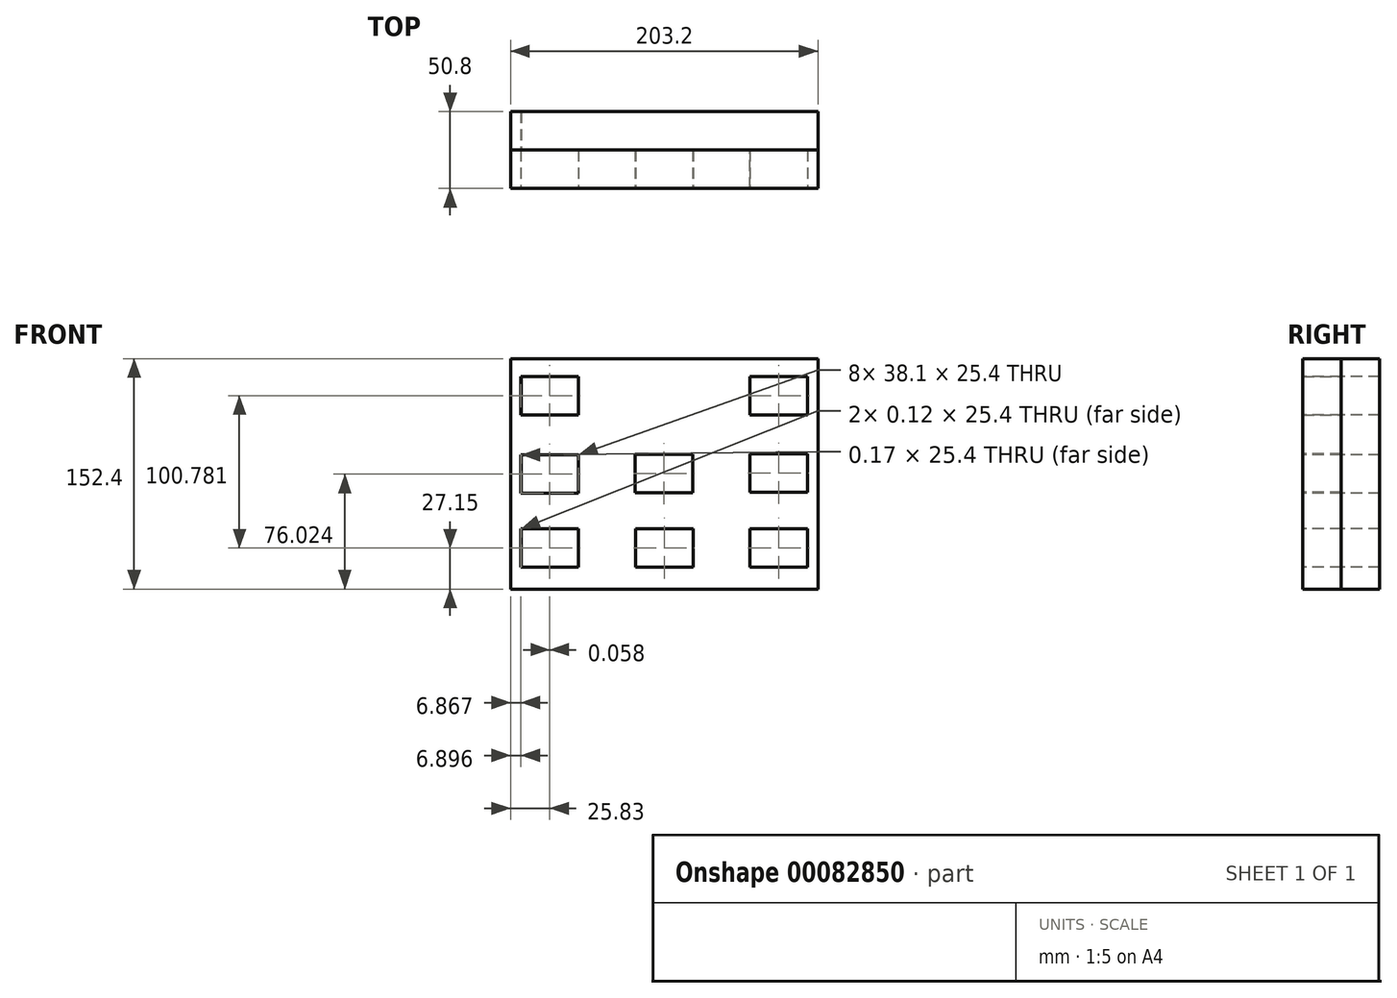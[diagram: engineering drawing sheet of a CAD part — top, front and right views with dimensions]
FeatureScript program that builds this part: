
annotation { "Feature Type Name" : "Feature", "Feature Type Description" : "" }
export const myFeature = defineFeature(function(context is Context, id is Id, definition is map)
    precondition{}
    {
        {
            var Q0;
            Q0=qCreatedBy(makeId("Front.planeOp"),FACE);
            var sketch = newSketch(context, id + "F0", { "sketchPlane" : qUnion([Q0])});
            skLineSegment(sketch, "E0.bottom", {"start": v(-101.6, 76.2) * mm, "end": v(101.6, 76.2) * mm});
            skLineSegment(sketch, "E0.top", {"start": v(-101.6, -76.2) * mm, "end": v(101.6, -76.2) * mm});
            skLineSegment(sketch, "E0.left", {"start": v(-101.6, 76.2) * mm, "end": v(-101.6, -76.2) * mm});
            skLineSegment(sketch, "E0.right", {"start": v(101.6, 76.2) * mm, "end": v(101.6, -76.2) * mm});
            skPoint(sketch, "E0.middle", {"position": v(0, 0) * mm});
            skSolve(sketch);
        }
        {
            var Q0;
            Q0 = qSketchRegion(id + "F0", true);
            extrude(context, id + "F1", {"entities" : qUnion([Q0]), "depth" : 25.4 * mm});
        }
        {
            var Q0;
            Q0=makeQuery(id+"F1.opExtrude","CAP_FACE",FACE,{"disambiguationData":[OSD([sQuery(id+"F0.wireOp",EDGE,"E0.bottom"),sQuery(id+"F0.wireOp",EDGE,"E0.top"),sQuery(id+"F0.wireOp",EDGE,"E0.left"),sQuery(id+"F0.wireOp",EDGE,"E0.right")])],"isStart":false});
            var sketch = newSketch(context, id + "F2", { "sketchPlane" : qUnion([Q0])});
            skLineSegment(sketch, "E1.bottom", {"start": v(-94.76, 64.43) * mm, "end": v(-56.66, 64.43) * mm});
            skLineSegment(sketch, "E1.top", {"start": v(-94.76, 39.03) * mm, "end": v(-56.66, 39.03) * mm});
            skLineSegment(sketch, "E1.left", {"start": v(-94.76, 64.43) * mm, "end": v(-94.76, 39.03) * mm});
            skLineSegment(sketch, "E1.right", {"start": v(-56.66, 64.43) * mm, "end": v(-56.66, 39.03) * mm});
            skPoint(sketch, "E1.middle", {"position": v(-75.71, 51.73) * mm});
            skLineSegment(sketch, "E2.1.0.0", {"start": v(-19.1, 64.43) * mm, "end": v(19, 64.43) * mm});
            skLineSegment(sketch, "E2.1.0.1", {"start": v(19, 64.43) * mm, "end": v(19, 39.03) * mm});
            skLineSegment(sketch, "E2.1.0.2", {"start": v(-19.1, 39.03) * mm, "end": v(19, 39.03) * mm});
            skLineSegment(sketch, "E2.1.0.3", {"start": v(-19.1, 64.43) * mm, "end": v(-19.1, 39.03) * mm});
            skPoint(sketch, "E2.1.0.4", {"position": v(-0.06, 51.73) * mm});
            skLineSegment(sketch, "E2.2.0.0", {"start": v(56.55, 64.43) * mm, "end": v(94.65, 64.43) * mm});
            skLineSegment(sketch, "E2.2.0.1", {"start": v(94.65, 64.43) * mm, "end": v(94.65, 39.03) * mm});
            skLineSegment(sketch, "E2.2.0.2", {"start": v(56.55, 39.03) * mm, "end": v(94.65, 39.03) * mm});
            skLineSegment(sketch, "E2.2.0.3", {"start": v(56.55, 64.43) * mm, "end": v(56.55, 39.03) * mm});
            skPoint(sketch, "E2.2.0.4", {"position": v(75.6, 51.73) * mm});
            skLineSegment(sketch, "E2.direction1", {"start": v(-94.76, 64.43) * mm, "end": v(-19.1, 64.43) * mm, "construction": true});
            skLineSegment(sketch, "E3.0.1.0", {"start": v(-94.76, -36.35) * mm, "end": v(-94.76, -61.75) * mm});
            skPoint(sketch, "E3.0.1.1", {"position": v(-75.71, -49.05) * mm});
            skLineSegment(sketch, "E3.0.1.2", {"start": v(-94.76, -36.35) * mm, "end": v(-56.66, -36.35) * mm});
            skLineSegment(sketch, "E3.0.1.3", {"start": v(-56.66, -36.35) * mm, "end": v(-56.66, -61.75) * mm});
            skLineSegment(sketch, "E3.0.1.4", {"start": v(-94.76, -61.75) * mm, "end": v(-56.66, -61.75) * mm});
            skLineSegment(sketch, "E3.0.2.0", {"start": v(-94.76, -137.13) * mm, "end": v(-94.76, -162.53) * mm});
            skPoint(sketch, "E3.0.2.1", {"position": v(-75.71, -149.83) * mm});
            skLineSegment(sketch, "E3.0.2.2", {"start": v(-94.76, -137.13) * mm, "end": v(-56.66, -137.13) * mm});
            skLineSegment(sketch, "E3.0.2.3", {"start": v(-56.66, -137.13) * mm, "end": v(-56.66, -162.53) * mm});
            skLineSegment(sketch, "E3.0.2.4", {"start": v(-94.76, -162.53) * mm, "end": v(-56.66, -162.53) * mm});
            skLineSegment(sketch, "E3.1.1.0", {"start": v(-19.1, -36.35) * mm, "end": v(-19.1, -61.75) * mm});
            skPoint(sketch, "E3.1.1.1", {"position": v(-0.06, -49.05) * mm});
            skLineSegment(sketch, "E3.1.1.2", {"start": v(-19.1, -36.35) * mm, "end": v(19, -36.35) * mm});
            skLineSegment(sketch, "E3.1.1.3", {"start": v(19, -36.35) * mm, "end": v(19, -61.75) * mm});
            skLineSegment(sketch, "E3.1.1.4", {"start": v(-19.1, -61.75) * mm, "end": v(19, -61.75) * mm});
            skLineSegment(sketch, "E3.1.2.0", {"start": v(-19.1, -137.13) * mm, "end": v(-19.1, -162.53) * mm});
            skPoint(sketch, "E3.1.2.1", {"position": v(-0.06, -149.83) * mm});
            skLineSegment(sketch, "E3.1.2.2", {"start": v(-19.1, -137.13) * mm, "end": v(19, -137.13) * mm});
            skLineSegment(sketch, "E3.1.2.3", {"start": v(19, -137.13) * mm, "end": v(19, -162.53) * mm});
            skLineSegment(sketch, "E3.1.2.4", {"start": v(-19.1, -162.53) * mm, "end": v(19, -162.53) * mm});
            skLineSegment(sketch, "E3.2.1.0", {"start": v(56.55, -36.35) * mm, "end": v(56.55, -61.75) * mm});
            skPoint(sketch, "E3.2.1.1", {"position": v(75.6, -49.05) * mm});
            skLineSegment(sketch, "E3.2.1.2", {"start": v(56.55, -36.35) * mm, "end": v(94.65, -36.35) * mm});
            skLineSegment(sketch, "E3.2.1.3", {"start": v(94.65, -36.35) * mm, "end": v(94.65, -61.75) * mm});
            skLineSegment(sketch, "E3.2.1.4", {"start": v(56.55, -61.75) * mm, "end": v(94.65, -61.75) * mm});
            skLineSegment(sketch, "E3.2.2.0", {"start": v(56.55, -137.13) * mm, "end": v(56.55, -162.53) * mm});
            skPoint(sketch, "E3.2.2.1", {"position": v(75.6, -149.83) * mm});
            skLineSegment(sketch, "E3.2.2.2", {"start": v(56.55, -137.13) * mm, "end": v(94.65, -137.13) * mm});
            skLineSegment(sketch, "E3.2.2.3", {"start": v(94.65, -137.13) * mm, "end": v(94.65, -162.53) * mm});
            skLineSegment(sketch, "E3.2.2.4", {"start": v(56.55, -162.53) * mm, "end": v(94.65, -162.53) * mm});
            skLineSegment(sketch, "E3.direction1", {"start": v(-94.76, 39.03) * mm, "end": v(-19.1, 39.03) * mm, "construction": true});
            skPoint(sketch, "E4.1.0.0", {"position": v(-75.77, -0.18) * mm});
            skLineSegment(sketch, "E4.1.0.1", {"start": v(-94.82, -12.88) * mm, "end": v(-56.72, -12.88) * mm});
            skLineSegment(sketch, "E4.1.0.2", {"start": v(-94.82, 12.52) * mm, "end": v(-94.82, -12.88) * mm});
            skLineSegment(sketch, "E4.1.0.3", {"start": v(-94.82, 12.52) * mm, "end": v(-56.72, 12.52) * mm});
            skLineSegment(sketch, "E4.1.0.4", {"start": v(-56.72, 12.52) * mm, "end": v(-56.72, -12.88) * mm});
            skLineSegment(sketch, "E4.direction1", {"start": v(-75.71, 51.73) * mm, "end": v(-75.77, -0.18) * mm, "construction": true});
            skPoint(sketch, "E5.1.0.0", {"position": v(-0.12, 0.15) * mm});
            skLineSegment(sketch, "E5.1.0.1", {"start": v(18.93, 12.85) * mm, "end": v(18.93, -12.55) * mm});
            skLineSegment(sketch, "E5.1.0.2", {"start": v(-19.17, 12.85) * mm, "end": v(18.93, 12.85) * mm});
            skLineSegment(sketch, "E5.1.0.3", {"start": v(-19.17, 12.85) * mm, "end": v(-19.17, -12.55) * mm});
            skLineSegment(sketch, "E5.1.0.4", {"start": v(-19.17, -12.55) * mm, "end": v(18.93, -12.55) * mm});
            skPoint(sketch, "E5.2.0.0", {"position": v(75.54, 0.49) * mm});
            skLineSegment(sketch, "E5.2.0.1", {"start": v(94.59, 13.19) * mm, "end": v(94.59, -12.21) * mm});
            skLineSegment(sketch, "E5.2.0.2", {"start": v(56.49, 13.19) * mm, "end": v(94.59, 13.19) * mm});
            skLineSegment(sketch, "E5.2.0.3", {"start": v(56.49, 13.19) * mm, "end": v(56.49, -12.21) * mm});
            skLineSegment(sketch, "E5.2.0.4", {"start": v(56.49, -12.21) * mm, "end": v(94.59, -12.21) * mm});
            skLineSegment(sketch, "E5.direction1", {"start": v(-75.77, -0.18) * mm, "end": v(-0.12, 0.15) * mm, "construction": true});
            skSolve(sketch);
        }
        {
            var Q0;
            Q0=makeQuery(id+"F2.imprint","IMPRINT",FACE,{"disambiguationData":[TD([[makeQuery(id+"F2.imprint","IMPRINT",EDGE,{"derivedFrom":sQuery(id+"F2.wireOp",EDGE,"E1.bottom")}),-1.0]])]});
            var Q1;
            Q1=makeQuery(id+"F2.imprint","IMPRINT",FACE,{"disambiguationData":[TD([[makeQuery(id+"F2.imprint","IMPRINT",EDGE,{"derivedFrom":sQuery(id+"F2.wireOp",EDGE,"E4.1.0.1")}),1.0]])]});
            var Q2;
            Q2=makeQuery(id+"F2.imprint","IMPRINT",FACE,{"disambiguationData":[TD([[makeQuery(id+"F2.imprint","IMPRINT",EDGE,{"derivedFrom":sQuery(id+"F2.wireOp",EDGE,"E2.1.0.3")}),1.0]])]});
            var Q3;
            Q3=makeQuery(id+"F2.imprint","IMPRINT",FACE,{"disambiguationData":[TD([[makeQuery(id+"F2.imprint","IMPRINT",EDGE,{"derivedFrom":sQuery(id+"F2.wireOp",EDGE,"E5.1.0.1")}),-1.0]])]});
            var Q4;
            Q4=makeQuery(id+"F2.imprint","IMPRINT",FACE,{"disambiguationData":[TD([[makeQuery(id+"F2.imprint","IMPRINT",EDGE,{"derivedFrom":sQuery(id+"F2.wireOp",EDGE,"E5.2.0.1")}),-1.0]])]});
            var Q5;
            {var subQ0=sQuery(id+"F2.wireOp",EDGE,"E2.2.0.3");Q5=makeQuery(id+"F2.imprint","IMPRINT",FACE,{"disambiguationData":[TD([[makeQuery(id+"F2.imprint","IMPRINT",EDGE,{"derivedFrom":subQ0}),1.0]])]});}
            var Q6;
            Q6=makeQuery(id+"F2.imprint","IMPRINT",FACE,{"disambiguationData":[TD([[makeQuery(id+"F2.imprint","IMPRINT",EDGE,{"derivedFrom":sQuery(id+"F2.wireOp",EDGE,"E3.2.1.0")}),1.0]])]});
            var Q7;
            Q7=makeQuery(id+"F2.imprint","IMPRINT",FACE,{"disambiguationData":[TD([[makeQuery(id+"F2.imprint","IMPRINT",EDGE,{"derivedFrom":sQuery(id+"F2.wireOp",EDGE,"E3.1.1.0")}),1.0]])]});
            var Q8;
            Q8=makeQuery(id+"F2.imprint","IMPRINT",FACE,{"disambiguationData":[TD([[makeQuery(id+"F2.imprint","IMPRINT",EDGE,{"derivedFrom":sQuery(id+"F2.wireOp",EDGE,"E3.0.1.0")}),1.0]])]});
            extrude(context, id + "F3", {"entities" : qUnion([Q0, Q1, Q2, Q3, Q4, Q5, Q6, Q7, Q8]), "operationType" : NewBodyOperationType.REMOVE, "oppositeDirection" : true, "depth" : 25.4 * mm});
        }
        {
            var Q0;
            Q0=makeQuery(id+"F1.opExtrude","CAP_FACE",FACE,{"disambiguationData":[OSD([sQuery(id+"F0.wireOp",EDGE,"E0.bottom"),sQuery(id+"F0.wireOp",EDGE,"E0.top"),sQuery(id+"F0.wireOp",EDGE,"E0.left"),sQuery(id+"F0.wireOp",EDGE,"E0.right")])],"isStart":true});
            var sketch = newSketch(context, id + "F4", { "sketchPlane" : qUnion([Q0])});
            skLineSegment(sketch, "E6.bottom", {"start": v(-94.65, 64.43) * mm, "end": v(94.65, 64.43) * mm});
            skLineSegment(sketch, "E6.top", {"start": v(-94.65, -64.43) * mm, "end": v(94.65, -64.43) * mm});
            skLineSegment(sketch, "E6.left", {"start": v(-94.65, 64.43) * mm, "end": v(-94.65, -64.43) * mm});
            skLineSegment(sketch, "E6.right", {"start": v(94.65, 64.43) * mm, "end": v(94.65, -64.43) * mm});
            skPoint(sketch, "E6.middle", {"position": v(0, 0) * mm});
            skSolve(sketch);
        }
        {
            var Q0;
            Q0 = qSketchRegion(id + "F4", true);
            var Q1;
            {var subQ5=sQuery(id+"F4.wireOp",EDGE,"E6.top");Q1=makeQuery(id+"F4.imprint","IMPRINT",FACE,{"disambiguationData":[TD([[makeQuery(id+"F4.imprint","IMPRINT",EDGE,{"derivedFrom":subQ5}),1.0]])]});}
            var Q2;
            {var subQ6=sQuery(id+"F4.wireOp",EDGE,"E6.top");Q2=makeQuery(id+"F4.imprint","IMPRINT",FACE,{"disambiguationData":[TD([[makeQuery(id+"F4.imprint","IMPRINT",EDGE,{"derivedFrom":subQ6}),-1.0]])]});}
            var Q3;
            Q3=makeQuery(id+"F4.imprint","IMPRINT",FACE,{"disambiguationData":[TD([[makeQuery(id+"F4.imprint","IMPRINT",EDGE,{"derivedFrom":makeQuery(id+"F3.boolean.opBoolean","COPY",EDGE,{"derivedFrom":makeQuery(id+"F3.opExtrude","CAP_EDGE",EDGE,{"disambiguationData":[OSD([sQuery(id+"F2.wireOp",EDGE,"E5.2.0.1")])],"isStart":false})})}),1.0]])]});
            var Q4;
            {var subQ3=makeQuery(id+"F3.boolean.opBoolean","COPY",EDGE,{"derivedFrom":makeQuery(id+"F3.opExtrude","CAP_EDGE",EDGE,{"disambiguationData":[OSD([sQuery(id+"F2.wireOp",EDGE,"E2.2.0.3")])],"isStart":false})});Q4=makeQuery(id+"F4.imprint","IMPRINT",FACE,{"disambiguationData":[TD([[makeQuery(id+"F4.imprint","IMPRINT",EDGE,{"derivedFrom":subQ3}),-1.0]])]});}
            var Q5;
            {var subQ1=makeQuery(id+"F3.boolean.opBoolean","COPY",EDGE,{"derivedFrom":makeQuery(id+"F3.opExtrude","CAP_EDGE",EDGE,{"disambiguationData":[OSD([sQuery(id+"F2.wireOp",EDGE,"E2.1.0.3")])],"isStart":false})});Q5=makeQuery(id+"F4.imprint","IMPRINT",FACE,{"disambiguationData":[TD([[makeQuery(id+"F4.imprint","IMPRINT",EDGE,{"derivedFrom":subQ1}),-1.0]])]});}
            var Q6;
            Q6=makeQuery(id+"F4.imprint","IMPRINT",FACE,{"disambiguationData":[TD([[makeQuery(id+"F4.imprint","IMPRINT",EDGE,{"derivedFrom":makeQuery(id+"F3.boolean.opBoolean","COPY",EDGE,{"derivedFrom":makeQuery(id+"F3.opExtrude","CAP_EDGE",EDGE,{"disambiguationData":[OSD([sQuery(id+"F2.wireOp",EDGE,"E5.1.0.1")])],"isStart":false})})}),1.0]])]});
            var Q7;
            {var subQ1=makeQuery(id+"F3.boolean.opBoolean","COPY",EDGE,{"derivedFrom":makeQuery(id+"F3.opExtrude","CAP_EDGE",EDGE,{"disambiguationData":[OSD([sQuery(id+"F2.wireOp",EDGE,"E1.right")])],"isStart":false})});Q7=makeQuery(id+"F4.imprint","IMPRINT",FACE,{"disambiguationData":[TD([[makeQuery(id+"F4.imprint","IMPRINT",EDGE,{"derivedFrom":subQ1}),1.0]])]});}
            var Q8;
            {var subQ5=makeQuery(id+"F3.boolean.opBoolean","COPY",EDGE,{"derivedFrom":makeQuery(id+"F3.opExtrude","CAP_EDGE",EDGE,{"disambiguationData":[OSD([sQuery(id+"F2.wireOp",EDGE,"E4.1.0.4")])],"isStart":false})});Q8=makeQuery(id+"F4.imprint","IMPRINT",FACE,{"disambiguationData":[TD([[makeQuery(id+"F4.imprint","IMPRINT",EDGE,{"derivedFrom":subQ5}),1.0]])]});}
            var Q9;
            {var subQ5=makeQuery(id+"F3.boolean.opBoolean","COPY",EDGE,{"derivedFrom":makeQuery(id+"F3.opExtrude","CAP_EDGE",EDGE,{"disambiguationData":[OSD([sQuery(id+"F2.wireOp",EDGE,"E3.0.1.3")])],"isStart":false})});Q9=makeQuery(id+"F4.imprint","IMPRINT",FACE,{"disambiguationData":[TD([[makeQuery(id+"F4.imprint","IMPRINT",EDGE,{"derivedFrom":subQ5}),1.0]])]});}
            var Q10;
            Q10=makeQuery(id+"F4.imprint","IMPRINT",FACE,{"disambiguationData":[TD([[makeQuery(id+"F4.imprint","IMPRINT",EDGE,{"derivedFrom":makeQuery(id+"F3.boolean.opBoolean","COPY",EDGE,{"derivedFrom":makeQuery(id+"F3.opExtrude","CAP_EDGE",EDGE,{"disambiguationData":[OSD([sQuery(id+"F2.wireOp",EDGE,"E3.1.1.0")])],"isStart":false})})}),-1.0]])]});
            var Q11;
            Q11=makeQuery(id+"F4.imprint","IMPRINT",FACE,{"disambiguationData":[TD([[makeQuery(id+"F4.imprint","IMPRINT",EDGE,{"derivedFrom":makeQuery(id+"F3.boolean.opBoolean","COPY",EDGE,{"derivedFrom":makeQuery(id+"F3.opExtrude","CAP_EDGE",EDGE,{"disambiguationData":[OSD([sQuery(id+"F2.wireOp",EDGE,"E3.2.1.0")])],"isStart":false})})}),-1.0]])]});
            extrude(context, id + "F5", {"entities" : qUnion([Q0, Q1, Q2, Q3, Q4, Q5, Q6, Q7, Q8, Q9, Q10, Q11]), "depth" : 25.4 * mm});
        }
    });
